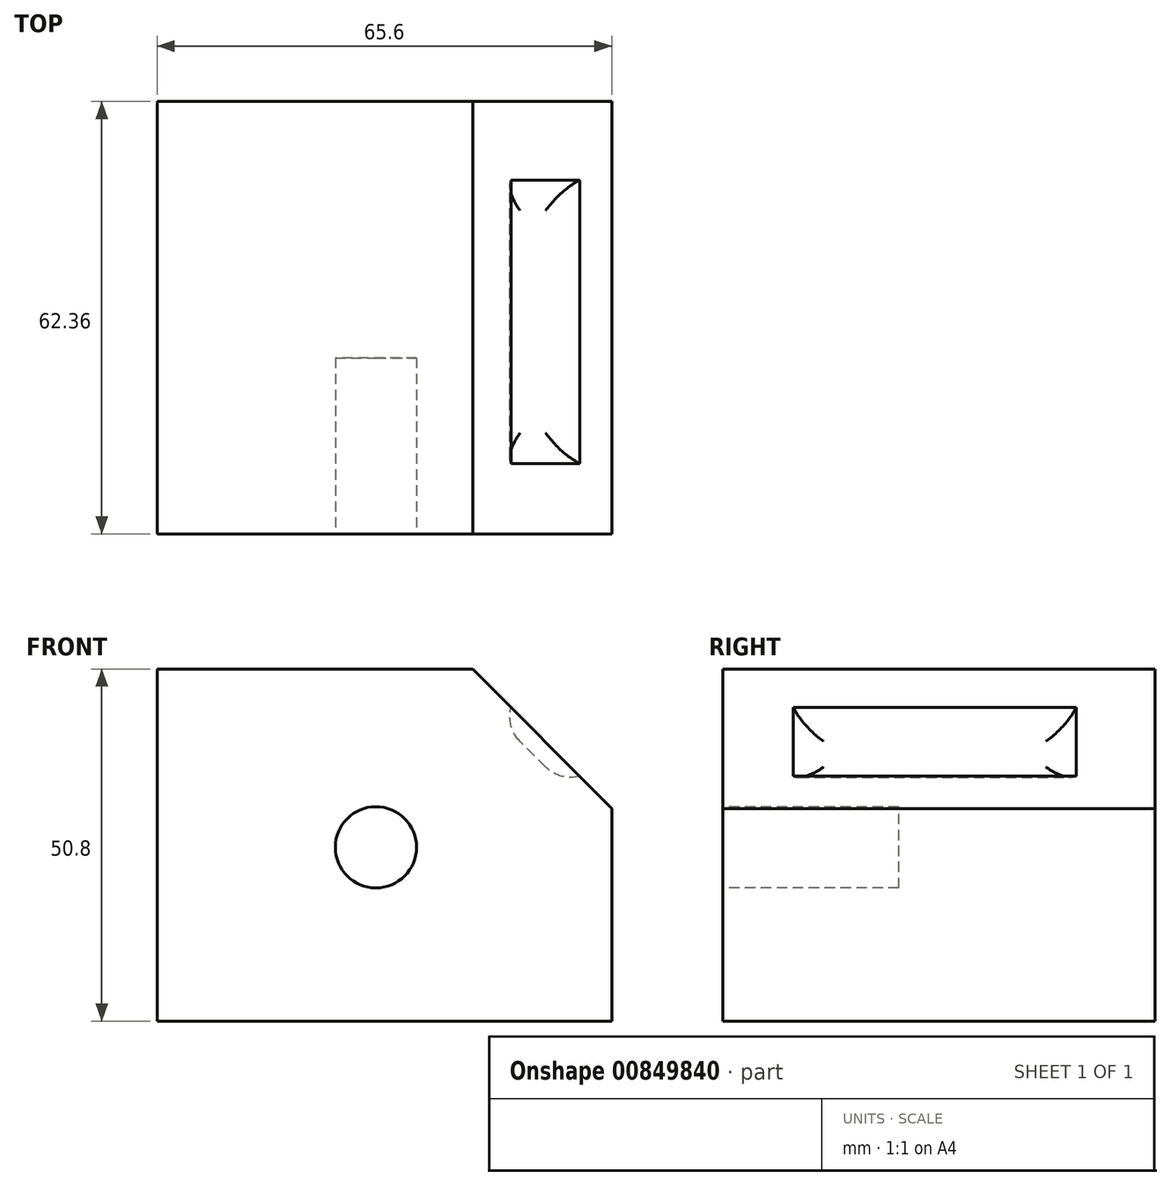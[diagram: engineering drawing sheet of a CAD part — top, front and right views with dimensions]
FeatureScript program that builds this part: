
annotation { "Feature Type Name" : "Feature", "Feature Type Description" : "" }
export const myFeature = defineFeature(function(context is Context, id is Id, definition is map)
    precondition{}
    {
        {
            var Q0;
            Q0=qCreatedBy(makeId("Top.planeOp"),FACE);
            var sketch = newSketch(context, id + "F0", { "sketchPlane" : qUnion([Q0])});
            skLineSegment(sketch, "E0.bottom", {"start": v(0, 0) * mm, "end": v(65.6, 0) * mm});
            skLineSegment(sketch, "E0.top", {"start": v(0, 62.36) * mm, "end": v(65.6, 62.36) * mm});
            skLineSegment(sketch, "E0.left", {"start": v(0, 0) * mm, "end": v(0, 62.36) * mm});
            skLineSegment(sketch, "E0.right", {"start": v(65.6, 0) * mm, "end": v(65.6, 62.36) * mm});
            skSolve(sketch);
        }
        {
            var Q0;
            Q0 = qSketchRegion(id + "F0", true);
            extrude(context, id + "F1", {"entities" : qUnion([Q0]), "depth" : 50.8 * mm, "offsetDistance" : 25.4 * mm});
        }
        {
            var Q0;
            Q0=makeQuery(id+"F1.opExtrude","SWEPT_FACE",FACE,{"disambiguationData":[OSD([sQuery(id+"F0.wireOp",EDGE,"E0.bottom")])]});
            var sketch = newSketch(context, id + "F2", { "sketchPlane" : qUnion([Q0])});
            skLineSegment(sketch, "E1", {"start": v(33.54, 62.93) * mm, "end": v(74.6, 21.58) * mm});
            skLineSegment(sketch, "E2", {"start": v(74.6, 21.58) * mm, "end": v(89.78, 45.49) * mm});
            skLineSegment(sketch, "E3", {"start": v(89.78, 45.49) * mm, "end": v(33.54, 62.93) * mm});
            skSolve(sketch);
        }
        {
            var Q0;
            Q0 = qSketchRegion(id + "F2", true);
            extrude(context, id + "F3", {"entities" : qUnion([Q0]), "operationType" : NewBodyOperationType.REMOVE, "oppositeDirection" : true, "depth" : 101.6 * mm, "offsetDistance" : 25.4 * mm});
        }
        {
            var Q0;
            Q0=makeQuery(id+"F3.boolean.opBoolean","COPY",FACE,{"derivedFrom":makeQuery(id+"F3.opExtrude","SWEPT_FACE",FACE,{"disambiguationData":[OSD([sQuery(id+"F2.wireOp",EDGE,"E1")])]})});
            var sketch = newSketch(context, id + "F4", { "sketchPlane" : qUnion([Q0])});
            skLineSegment(sketch, "E4.bottom", {"start": v(10.15, -3.86) * mm, "end": v(51.03, -3.86) * mm});
            skLineSegment(sketch, "E4.top", {"start": v(10.15, -17.9) * mm, "end": v(51.03, -17.9) * mm});
            skLineSegment(sketch, "E4.left", {"start": v(10.15, -3.86) * mm, "end": v(10.15, -17.9) * mm});
            skLineSegment(sketch, "E4.right", {"start": v(51.03, -3.86) * mm, "end": v(51.03, -17.9) * mm});
            skSolve(sketch);
        }
        {
            var Q0;
            Q0 = qSketchRegion(id + "F4", true);
            extrude(context, id + "F5", {"entities" : qUnion([Q0]), "operationType" : NewBodyOperationType.REMOVE, "oppositeDirection" : true, "depth" : 2.54 * mm, "offsetDistance" : 25.4 * mm});
        }
        {
            var Q0;
            Q0=makeQuery(id+"F1.opExtrude","SWEPT_FACE",FACE,{"disambiguationData":[OSD([sQuery(id+"F0.wireOp",EDGE,"E0.bottom")])]});
            var sketch = newSketch(context, id + "F6", { "sketchPlane" : qUnion([Q0])});
            skCircle(sketch, "E5", {"center": v(31.57, 25.06) * mm, "radius": 5.86 * mm});
            skSolve(sketch);
        }
        {
            var Q0;
            Q0 = qSketchRegion(id + "F6", true);
            extrude(context, id + "F7", {"entities" : qUnion([Q0]), "operationType" : NewBodyOperationType.REMOVE, "oppositeDirection" : true, "depth" : 25.4 * mm, "offsetDistance" : 25.4 * mm});
        }
        {
            var Q0;
            Q0=makeQuery(id+"F5.boolean.opBoolean","COPY",EDGE,{"derivedFrom":makeQuery(id+"F5.opExtrude","CAP_EDGE",EDGE,{"disambiguationData":[OSD([sQuery(id+"F4.wireOp",EDGE,"E4.bottom")])],"isStart":false})});
            var Q1;
            Q1=makeQuery(id+"F5.boolean.opBoolean","COPY",EDGE,{"derivedFrom":makeQuery(id+"F5.opExtrude","CAP_EDGE",EDGE,{"disambiguationData":[OSD([sQuery(id+"F4.wireOp",EDGE,"E4.right")])],"isStart":false})});
            var Q2;
            Q2=makeQuery(id+"F5.boolean.opBoolean","COPY",EDGE,{"derivedFrom":makeQuery(id+"F5.opExtrude","CAP_EDGE",EDGE,{"disambiguationData":[OSD([sQuery(id+"F4.wireOp",EDGE,"E4.top")])],"isStart":false})});
            var Q3;
            Q3=makeQuery(id+"F5.boolean.opBoolean","COPY",EDGE,{"derivedFrom":makeQuery(id+"F5.opExtrude","CAP_EDGE",EDGE,{"disambiguationData":[OSD([sQuery(id+"F4.wireOp",EDGE,"E4.left")])],"isStart":false})});
            fillet(context, id + "F8", {"entities" : qUnion([Q0, Q1, Q2, Q3]), "radius" : 5.08 * mm, "tangentPropagation" : true, "allowEdgeOverflow" : false});
        }
    });
